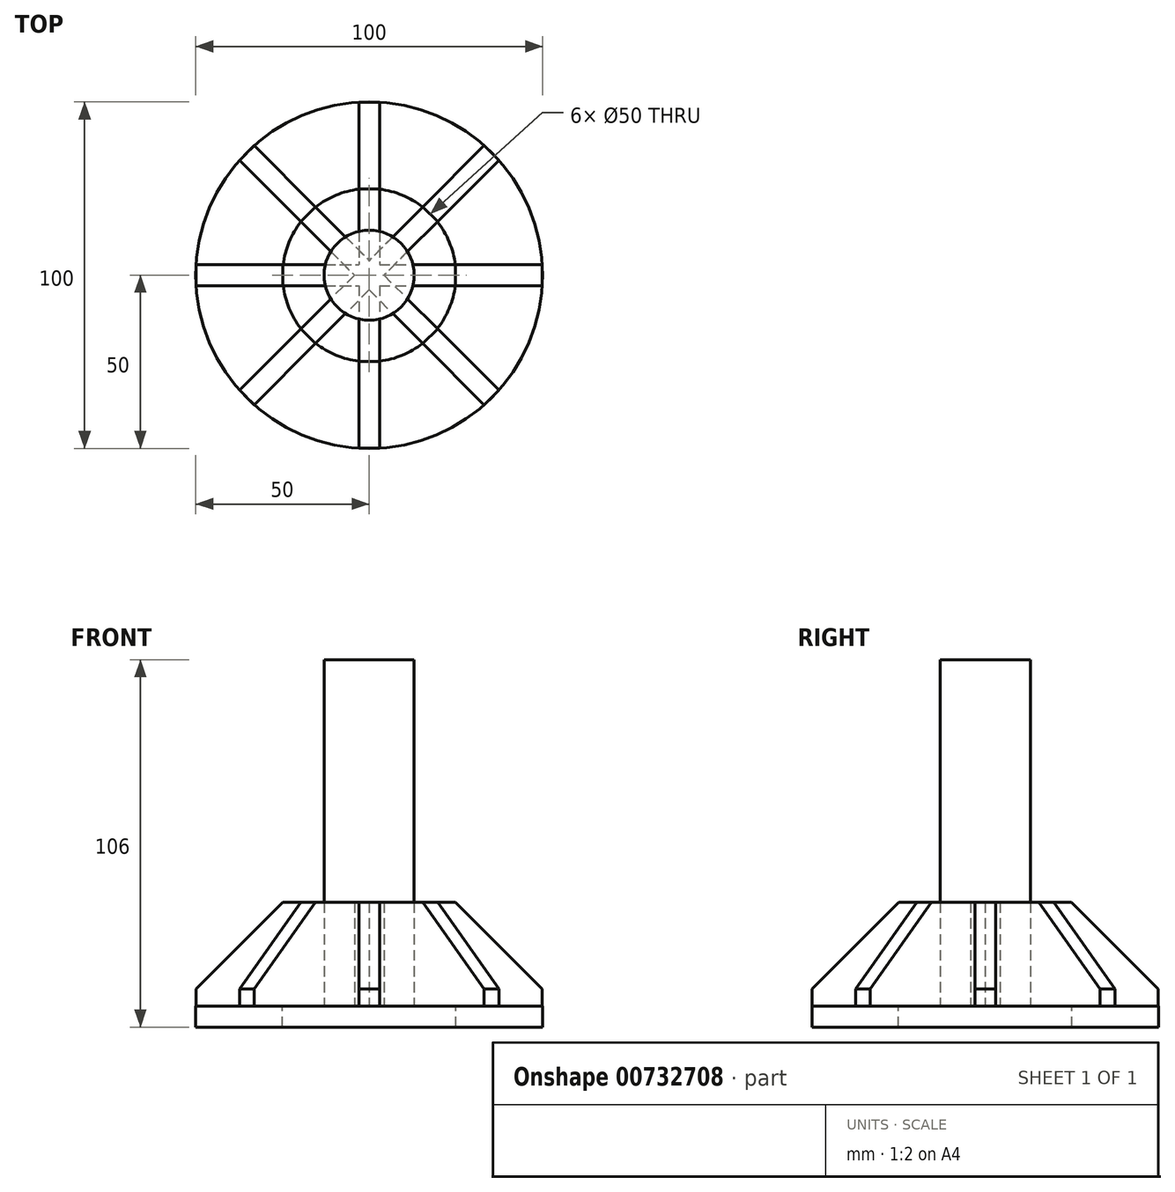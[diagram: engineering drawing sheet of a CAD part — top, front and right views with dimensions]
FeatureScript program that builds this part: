
annotation { "Feature Type Name" : "Feature", "Feature Type Description" : "" }
export const myFeature = defineFeature(function(context is Context, id is Id, definition is map)
    precondition{}
    {
        {
            var Q0;
            Q0=qCreatedBy(makeId("Top.planeOp"),FACE);
            var sketch = newSketch(context, id + "F0", { "sketchPlane" : qUnion([Q0])});
            skCircle(sketch, "E0", {"center": v(0, 0) * mm, "radius": 50 * mm});
            skSolve(sketch);
        }
        {
            var Q0;
            Q0 = qSketchRegion(id + "F0", true);
            extrude(context, id + "F1", {"entities" : qUnion([Q0]), "oppositeDirection" : true, "depth" : 6 * mm, "offsetDistance" : 25 * mm});
        }
        {
            var Q0;
            Q0=qCreatedBy(makeId("Top.planeOp"),FACE);
            var sketch = newSketch(context, id + "F2", { "sketchPlane" : qUnion([Q0])});
            skCircle(sketch, "E1", {"center": v(0, 0) * mm, "radius": 25 * mm});
            skSolve(sketch);
        }
        {
            var Q0;
            Q0 = qSketchRegion(id + "F2", true);
            extrude(context, id + "F3", {"entities" : qUnion([Q0]), "operationType" : NewBodyOperationType.REMOVE, "oppositeDirection" : true, "depth" : 6 * mm, "offsetDistance" : 25 * mm});
        }
        {
            var Q0;
            Q0=qCreatedBy(makeId("Top.planeOp"),FACE);
            var sketch = newSketch(context, id + "F4", { "sketchPlane" : qUnion([Q0])});
            skCircle(sketch, "E2", {"center": v(0, 0) * mm, "radius": 25 * mm});
            skSolve(sketch);
        }
        {
            var Q0;
            Q0 = qSketchRegion(id + "F4", true);
            extrude(context, id + "F5", {"entities" : qUnion([Q0]), "oppositeDirection" : true, "depth" : 6 * mm, "offsetDistance" : 25 * mm});
        }
        {
            var Q0;
            Q0=qCreatedBy(makeId("Top.planeOp"),FACE);
            var sketch = newSketch(context, id + "F6", { "sketchPlane" : qUnion([Q0])});
            skCircle(sketch, "E3", {"center": v(0, 0) * mm, "radius": 13 * mm});
            skSolve(sketch);
        }
        {
            var Q0;
            Q0 = qSketchRegion(id + "F6", true);
            extrude(context, id + "F7", {"entities" : qUnion([Q0]), "depth" : 100 * mm, "offsetDistance" : 25 * mm});
        }
        {
            var Q0;
            Q0=qCreatedBy(makeId("Top.planeOp"),FACE);
            var sketch = newSketch(context, id + "F8", { "sketchPlane" : qUnion([Q0])});
            skLineSegment(sketch, "E4.bottom", {"start": v(-49.9, 3) * mm, "end": v(49.9, 3) * mm});
            skLineSegment(sketch, "E4.top", {"start": v(-49.9, -3) * mm, "end": v(49.9, -3) * mm});
            skLineSegment(sketch, "E4.left", {"start": v(-49.9, 3) * mm, "end": v(-49.9, -3) * mm});
            skLineSegment(sketch, "E4.right", {"start": v(49.9, 3) * mm, "end": v(49.9, -3) * mm});
            skPoint(sketch, "E4.middle", {"position": v(0, 0) * mm});
            skLineSegment(sketch, "E5.bottom", {"start": v(-3, 49.9) * mm, "end": v(3, 49.9) * mm});
            skLineSegment(sketch, "E5.top", {"start": v(-3, -49.9) * mm, "end": v(3, -49.9) * mm});
            skLineSegment(sketch, "E5.left", {"start": v(-3, 49.9) * mm, "end": v(-3, -49.9) * mm});
            skLineSegment(sketch, "E5.right", {"start": v(3, 49.9) * mm, "end": v(3, -49.9) * mm});
            skSolve(sketch);
        }
        {
            var Q0;
            Q0 = qSketchRegion(id + "F8", true);
            extrude(context, id + "F9", {"entities" : qUnion([Q0]), "depth" : 30 * mm, "offsetDistance" : 25 * mm});
        }
        {
            var Q0;
            Q0=makeQuery(id+"F9.opExtrude","CAP_EDGE",EDGE,{"disambiguationData":[OSD([sQuery(id+"F8.wireOp",EDGE,"E4.left")])],"isStart":false});
            var Q1;
            Q1=makeQuery(id+"F9.opExtrude","CAP_EDGE",EDGE,{"disambiguationData":[OSD([sQuery(id+"F8.wireOp",EDGE,"E5.top")])],"isStart":false});
            var Q2;
            Q2=makeQuery(id+"F9.opExtrude","CAP_EDGE",EDGE,{"disambiguationData":[OSD([sQuery(id+"F8.wireOp",EDGE,"E4.right")])],"isStart":false});
            var Q3;
            Q3=makeQuery(id+"F9.opExtrude","CAP_EDGE",EDGE,{"disambiguationData":[OSD([sQuery(id+"F8.wireOp",EDGE,"E5.bottom")])],"isStart":false});
            chamfer(context, id + "F10", {"entities" : qUnion([Q0, Q1, Q2, Q3]), "width" : 25 * mm, "tangentPropagation" : true});
        }
        {
            var Q0;
            Q0=qCreatedBy(makeId("Front.planeOp"),FACE);
            var sketch = newSketch(context, id + "F11", { "sketchPlane" : qUnion([Q0])});
            skLineSegment(sketch, "E6", {"start": v(0, 0) * mm, "end": v(0, -47.39) * mm});
            skSolve(sketch);
        }
        {
            var Q0;
            Q0=makeQuery(id+"F9.opExtrude","SWEPT_BODY",BODY,{"disambiguationData":[OSD([sQuery(id+"F8.wireOp",EDGE,"E4.bottom"),sQuery(id+"F8.wireOp",EDGE,"E4.top"),sQuery(id+"F8.wireOp",EDGE,"E4.left"),sQuery(id+"F8.wireOp",EDGE,"E4.right"),sQuery(id+"F8.wireOp",EDGE,"E5.bottom"),sQuery(id+"F8.wireOp",EDGE,"E5.top"),sQuery(id+"F8.wireOp",EDGE,"E5.left"),sQuery(id+"F8.wireOp",EDGE,"E5.right")])]});
            var Q1;
            Q1=sQuery(id+"F11.wireOp",EDGE,"E6");
            transform(context, id + "F12", {"entities" : qUnion([Q0]), "transformType" : TransformType.ROTATION, "transformAxis" : qUnion([Q1]), "angle" : 45 * degree, "makeCopy" : true});
        }
    });
